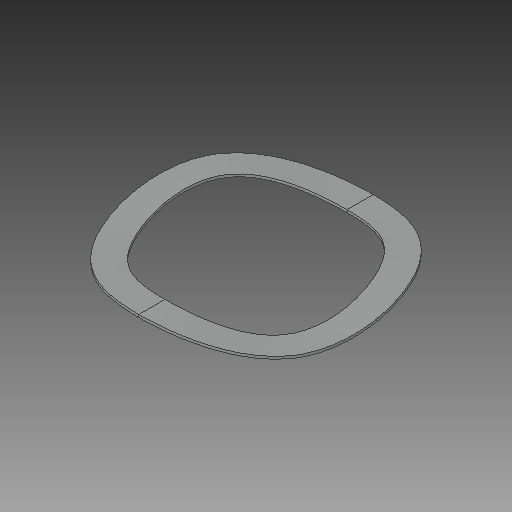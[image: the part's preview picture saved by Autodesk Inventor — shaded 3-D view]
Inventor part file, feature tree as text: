
AUTODESK INVENTOR PART (.ipt)
format: ipt  version: 2019 (Build 230136000, 136)  size: 124,416 bytes
history: native  units: in
note: dims shown in document units (in); Inventor stores cm internally (conversion verified against a paired STEP export)
features: loft x1
ambient origin geometry x8: Origin, YZ Plane, XZ Plane, XY Plane, X Axis, Y Axis, Z Axis, Center Point
bodies: Solid1 (feature_tree)
feature tree (1):
  loft  "Loft1"
